# Revit family: Hekatron_Brandmeldetechnik_ORS 155 F _DE_23.01
name_source: partatom
category: Brandmelder
revit_build: Autodesk Revit 2018 (Build: 20170223_1515(x64)
units: mm (PartAtom-declared; Revit-internal decimal feet)

## family parameters
Basisbauteil = Fläche
Beim Laden mit Abzugskörper schneiden = Nein
Bemaßung runder Anschluss = Durchmesser verwenden
Beschriftungsausrichtung beibehalten = Ja
Gemeinsam genutzt = Nein
OmniClass-Nummer = 23.85.30.21
OmniClass-Titel = Environmental Detection/Registration
Raumberechnungspunkt = Nein
Teiletyp = Normal

## types (1)
- ORS 155 F
    Beschreibung = Optischer Funkrauchschalter zum Einsatz in Feststellanlagen und weiteren Anwendungen.
    Betriebsspannung = 3 V DC
    Durchmesser (mm) = 80.0
    EG-Konformitaetszertifikat / Zertifikat der Leistungsbestaendigkeit = 1772-CPR-200341
    Farbe = weiß, ähnlich RAL 9010
    Hersteller = Hekatron
    Hoehe (mm) = 70.0
    Leistungserklaerung (DoP) = CRP-31-20-001
    Link zu Ausschreibungstext = https://www.meinhplus.de
    Link zu Produktinformation = https://www.hekatron-brandschutz.de
    Link zu ausschreiben.de = https://ausschreiben.de
    Link zum Datenblatt = https://www.hekatron-brandschutz.de
    Material = Polycarbonat
    Modell = ORS 155 F
    Montageart = Decke
    Nettogewicht (g) = 168.0
    Schutzart = IP 42
    Typenkommentare = Optischer Funkrauchschalter weiß
    UB A&S Artikel Nummer = 31-5000026-01-03
    URL = www.hekatron-brandschutz.de
    Version des BIM Objektes = 23.01
    Vorgabe-Ansicht = 1200 mm
    Zulaessige Umgebungstemperatur = -30 °C bis 70 °C
    Zulassungen nach EN 54 = 54-7, 54-25

## geometry (parser evidence)
native form markers: Sweep x2
no freeform markers — native parametric forms only
